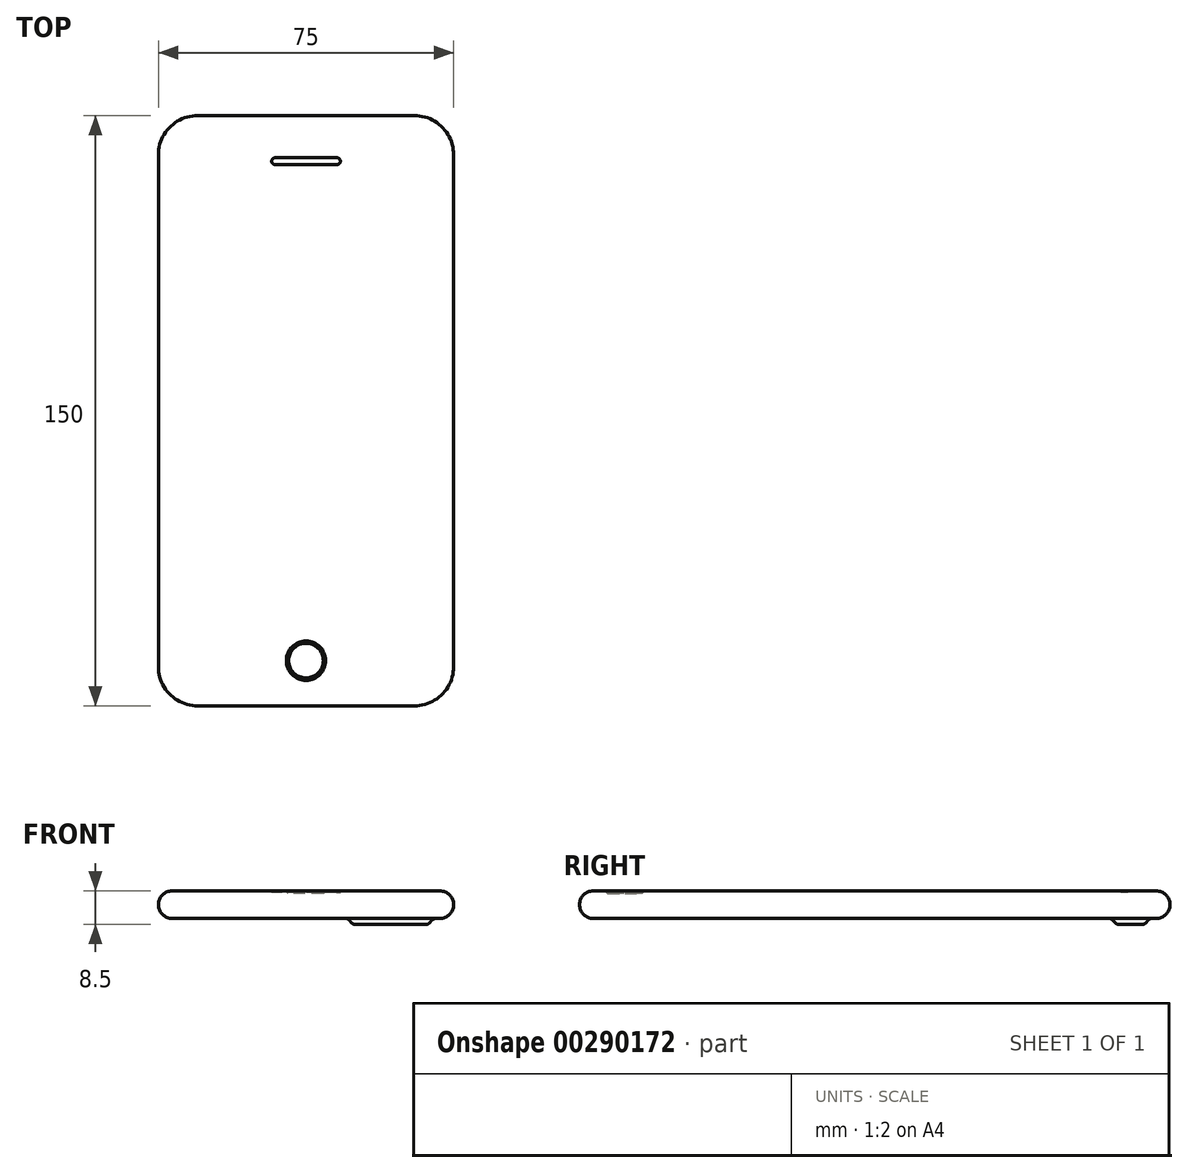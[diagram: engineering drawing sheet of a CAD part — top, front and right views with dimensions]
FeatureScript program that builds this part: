
annotation { "Feature Type Name" : "Feature", "Feature Type Description" : "" }
export const myFeature = defineFeature(function(context is Context, id is Id, definition is map)
    precondition{}
    {
        {
            var Q0;
            Q0=qCreatedBy(makeId("Top.planeOp"),FACE);
            var sketch = newSketch(context, id + "F0", { "sketchPlane" : qUnion([Q0])});
            skLineSegment(sketch, "E0.bottom", {"start": v(37.5, -75) * mm, "end": v(-37.5, -75) * mm});
            skLineSegment(sketch, "E0.top", {"start": v(37.5, 75) * mm, "end": v(-37.5, 75) * mm});
            skLineSegment(sketch, "E0.left", {"start": v(37.5, -75) * mm, "end": v(37.5, 75) * mm});
            skLineSegment(sketch, "E0.right", {"start": v(-37.5, -75) * mm, "end": v(-37.5, 75) * mm});
            skPoint(sketch, "E0.middle", {"position": v(0, 0) * mm});
            skSolve(sketch);
        }
        {
            var Q0;
            Q0 = qSketchRegion(id + "F0", true);
            extrude(context, id + "F1", {"entities" : qUnion([Q0]), "depth" : 7 * mm});
        }
        {
            var Q0;
            Q0=makeQuery(id+"F1.opExtrude","SWEPT_EDGE",EDGE,{"disambiguationData":[OSD([sQuery(id+"F0.wireOp",EDGE,"E0.bottom"),sQuery(id+"F0.wireOp",EDGE,"E0.right")])]});
            var Q1;
            Q1=makeQuery(id+"F1.opExtrude","SWEPT_EDGE",EDGE,{"disambiguationData":[OSD([sQuery(id+"F0.wireOp",EDGE,"E0.bottom"),sQuery(id+"F0.wireOp",EDGE,"E0.left")])]});
            var Q2;
            Q2=makeQuery(id+"F1.opExtrude","SWEPT_EDGE",EDGE,{"disambiguationData":[OSD([sQuery(id+"F0.wireOp",EDGE,"E0.top"),sQuery(id+"F0.wireOp",EDGE,"E0.left")])]});
            var Q3;
            Q3=makeQuery(id+"F1.opExtrude","SWEPT_EDGE",EDGE,{"disambiguationData":[OSD([sQuery(id+"F0.wireOp",EDGE,"E0.top"),sQuery(id+"F0.wireOp",EDGE,"E0.right")])]});
            fillet(context, id + "F2", {"entities" : qUnion([Q0, Q1, Q2, Q3]), "radius" : 10 * mm, "tangentPropagation" : true, "allowEdgeOverflow" : false});
        }
        {
            var Q0;
            Q0=makeQuery(id+"F1.opExtrude","CAP_FACE",FACE,{"disambiguationData":[OSD([sQuery(id+"F0.wireOp",EDGE,"E0.bottom"),sQuery(id+"F0.wireOp",EDGE,"E0.top"),sQuery(id+"F0.wireOp",EDGE,"E0.left"),sQuery(id+"F0.wireOp",EDGE,"E0.right")])],"isStart":true});
            var Q1;
            Q1=makeQuery(id+"F1.opExtrude","CAP_FACE",FACE,{"disambiguationData":[OSD([sQuery(id+"F0.wireOp",EDGE,"E0.bottom"),sQuery(id+"F0.wireOp",EDGE,"E0.top"),sQuery(id+"F0.wireOp",EDGE,"E0.left"),sQuery(id+"F0.wireOp",EDGE,"E0.right")])],"isStart":false});
            fillet(context, id + "F3", {"entities" : qUnion([Q0, Q1]), "radius" : 3.5 * mm, "tangentPropagation" : true, "allowEdgeOverflow" : false});
        }
        {
            var Q0;
            Q0=makeQuery(id+"F1.opExtrude","CAP_FACE",FACE,{"disambiguationData":[OSD([sQuery(id+"F0.wireOp",EDGE,"E0.bottom"),sQuery(id+"F0.wireOp",EDGE,"E0.top"),sQuery(id+"F0.wireOp",EDGE,"E0.left"),sQuery(id+"F0.wireOp",EDGE,"E0.right")])],"isStart":false});
            var sketch = newSketch(context, id + "F4", { "sketchPlane" : qUnion([Q0])});
            skCircle(sketch, "E1", {"center": v(0, -63.5) * mm, "radius": 5 * mm});
            skSolve(sketch);
        }
        {
            var Q0;
            Q0 = qSketchRegion(id + "F4", true);
            extrude(context, id + "F5", {"entities" : qUnion([Q0]), "operationType" : NewBodyOperationType.REMOVE, "oppositeDirection" : true, "depth" : 0.6 * mm});
        }
        {
            var Q0;
            Q0=makeQuery(id+"F5.boolean.opBoolean","COPY",FACE,{"derivedFrom":makeQuery(id+"F5.opExtrude","CAP_FACE",FACE,{"disambiguationData":[OSD([sQuery(id+"F4.wireOp",EDGE,"E1")])],"isStart":false})});
            chamfer(context, id + "F6", {"entities" : qUnion([Q0]), "width" : .6 * mm, "tangentPropagation" : true});
        }
        {
            var Q0;
            Q0=makeQuery(id+"F1.opExtrude","CAP_FACE",FACE,{"disambiguationData":[OSD([sQuery(id+"F0.wireOp",EDGE,"E0.bottom"),sQuery(id+"F0.wireOp",EDGE,"E0.top"),sQuery(id+"F0.wireOp",EDGE,"E0.left"),sQuery(id+"F0.wireOp",EDGE,"E0.right")])],"isStart":false});
            var sketch = newSketch(context, id + "F7", { "sketchPlane" : qUnion([Q0])});
            skLineSegment(sketch, "E2.bottom", {"start": v(8.75, 64.3) * mm, "end": v(-8.75, 64.3) * mm});
            skLineSegment(sketch, "E2.top", {"start": v(8.75, 62.5) * mm, "end": v(-8.75, 62.5) * mm});
            skLineSegment(sketch, "E2.left", {"start": v(8.75, 64.3) * mm, "end": v(8.75, 62.5) * mm});
            skLineSegment(sketch, "E2.right", {"start": v(-8.75, 64.3) * mm, "end": v(-8.75, 62.5) * mm});
            skPoint(sketch, "E2.middle", {"position": v(0, 63.4) * mm});
            skSolve(sketch);
        }
        {
            var Q0;
            Q0 = qSketchRegion(id + "F7", true);
            extrude(context, id + "F8", {"entities" : qUnion([Q0]), "operationType" : NewBodyOperationType.REMOVE, "oppositeDirection" : true, "depth" : .4 * mm});
        }
        {
            var Q0;
            Q0=makeQuery(id+"F8.boolean.opBoolean","COPY",EDGE,{"derivedFrom":makeQuery(id+"F8.opExtrude","SWEPT_EDGE",EDGE,{"disambiguationData":[OSD([sQuery(id+"F7.wireOp",EDGE,"E2.bottom"),sQuery(id+"F7.wireOp",EDGE,"E2.left")])]})});
            var Q1;
            Q1=makeQuery(id+"F8.boolean.opBoolean","COPY",EDGE,{"derivedFrom":makeQuery(id+"F8.opExtrude","SWEPT_EDGE",EDGE,{"disambiguationData":[OSD([sQuery(id+"F7.wireOp",EDGE,"E2.top"),sQuery(id+"F7.wireOp",EDGE,"E2.left")])]})});
            var Q2;
            Q2=makeQuery(id+"F8.boolean.opBoolean","COPY",EDGE,{"derivedFrom":makeQuery(id+"F8.opExtrude","SWEPT_EDGE",EDGE,{"disambiguationData":[OSD([sQuery(id+"F7.wireOp",EDGE,"E2.bottom"),sQuery(id+"F7.wireOp",EDGE,"E2.right")])]})});
            var Q3;
            Q3=makeQuery(id+"F8.boolean.opBoolean","COPY",EDGE,{"derivedFrom":makeQuery(id+"F8.opExtrude","SWEPT_EDGE",EDGE,{"disambiguationData":[OSD([sQuery(id+"F7.wireOp",EDGE,"E2.top"),sQuery(id+"F7.wireOp",EDGE,"E2.right")])]})});
            fillet(context, id + "F9", {"entities" : qUnion([Q0, Q1, Q2, Q3]), "radius" : 1 * mm, "tangentPropagation" : true, "allowEdgeOverflow" : false});
        }
        {
            var Q0;
            Q0=makeQuery(id+"F1.opExtrude","CAP_FACE",FACE,{"disambiguationData":[OSD([sQuery(id+"F0.wireOp",EDGE,"E0.bottom"),sQuery(id+"F0.wireOp",EDGE,"E0.top"),sQuery(id+"F0.wireOp",EDGE,"E0.left"),sQuery(id+"F0.wireOp",EDGE,"E0.right")])],"isStart":true});
            var sketch = newSketch(context, id + "F10", { "sketchPlane" : qUnion([Q0])});
            skLineSegment(sketch, "E3.bottom", {"start": v(15.5, -70) * mm, "end": v(27.5, -70) * mm});
            skLineSegment(sketch, "E3.top", {"start": v(15.5, -60) * mm, "end": v(27.5, -60) * mm});
            skLineSegment(sketch, "E3.left", {"start": v(10.5, -65) * mm, "end": v(10.5, -65) * mm});
            skLineSegment(sketch, "E3.right", {"start": v(32.5, -65) * mm, "end": v(32.5, -65) * mm});
            skPoint(sketch, "E3.middle", {"position": v(21.5, -65) * mm});
            skPoint(sketch, "E4.visualSharp", {"position": v(32.5, -70) * mm});
            skArc(sketch, "E4.filletArc", {"start": v(27.5, -70) * mm, "mid": v(31.04, -68.54) * mm, "end": v(32.5, -65) * mm});
            skPoint(sketch, "E5.visualSharp", {"position": v(32.5, -60) * mm});
            skArc(sketch, "E5.filletArc", {"start": v(32.5, -65) * mm, "mid": v(31.04, -61.46) * mm, "end": v(27.5, -60) * mm});
            skPoint(sketch, "E6.visualSharp", {"position": v(10.5, -70) * mm});
            skArc(sketch, "E6.filletArc", {"start": v(10.5, -65) * mm, "mid": v(11.96, -68.54) * mm, "end": v(15.5, -70) * mm});
            skPoint(sketch, "E7.visualSharp", {"position": v(10.5, -60) * mm});
            skArc(sketch, "E7.filletArc", {"start": v(15.5, -60) * mm, "mid": v(11.96, -61.46) * mm, "end": v(10.5, -65) * mm});
            skSolve(sketch);
        }
        {
            var Q0;
            Q0 = qSketchRegion(id + "F10", true);
            extrude(context, id + "F11", {"entities" : qUnion([Q0]), "operationType" : NewBodyOperationType.ADD, "depth" : 1.5 * mm});
        }
        {
            var Q0;
            Q0=makeQuery(id+"F11.opExtrude","CAP_EDGE",EDGE,{"disambiguationData":[OSD([sQuery(id+"F10.wireOp",EDGE,"E3.bottom")])],"isStart":false});
            chamfer(context, id + "F12", {"entities" : qUnion([Q0]), "width" : 1.5 * mm, "tangentPropagation" : true});
        }
        {
            var Q0;
            Q0=makeQuery(id+"F12.opChamfer","BLEND_EDGE",EDGE,{"blendedFrom":[makeQuery(id+"F11.opExtrude","CAP_EDGE",EDGE,{"disambiguationData":[OSD([sQuery(id+"F10.wireOp",EDGE,"E3.bottom")])],"isStart":false}),makeQuery(id+"F1.opExtrude","CAP_FACE",FACE,{"disambiguationData":[OSD([sQuery(id+"F0.wireOp",EDGE,"E0.bottom"),sQuery(id+"F0.wireOp",EDGE,"E0.top"),sQuery(id+"F0.wireOp",EDGE,"E0.left"),sQuery(id+"F0.wireOp",EDGE,"E0.right")])],"isStart":true})],"blendedInto":[makeQuery(id+"F1.opExtrude","CAP_FACE",FACE,{"disambiguationData":[OSD([sQuery(id+"F0.wireOp",EDGE,"E0.bottom"),sQuery(id+"F0.wireOp",EDGE,"E0.top"),sQuery(id+"F0.wireOp",EDGE,"E0.left"),sQuery(id+"F0.wireOp",EDGE,"E0.right")])],"isStart":true})]});
            var Q1;
            {var subQ0=sQuery(id+"F10.wireOp",EDGE,"E3.bottom");Q1=makeQuery(id+"F12.opChamfer","BLEND_EDGE",EDGE,{"blendedFrom":[makeQuery(id+"F11.opExtrude","CAP_EDGE",EDGE,{"disambiguationData":[OSD([subQ0])],"isStart":false}),makeQuery(id+"F11.opExtrude","CAP_FACE",FACE,{"disambiguationData":[OSD([subQ0,sQuery(id+"F10.wireOp",EDGE,"E3.top"),sQuery(id+"F10.wireOp",EDGE,"E4.filletArc"),sQuery(id+"F10.wireOp",EDGE,"E5.filletArc"),sQuery(id+"F10.wireOp",EDGE,"E6.filletArc"),sQuery(id+"F10.wireOp",EDGE,"E7.filletArc")])],"isStart":false})],"blendedInto":[makeQuery(id+"F11.opExtrude","CAP_FACE",FACE,{"disambiguationData":[OSD([subQ0,sQuery(id+"F10.wireOp",EDGE,"E3.top"),sQuery(id+"F10.wireOp",EDGE,"E4.filletArc"),sQuery(id+"F10.wireOp",EDGE,"E5.filletArc"),sQuery(id+"F10.wireOp",EDGE,"E6.filletArc"),sQuery(id+"F10.wireOp",EDGE,"E7.filletArc")])],"isStart":false})]});}
            fillet(context, id + "F13", {"entities" : qUnion([Q0, Q1]), "radius" : 1 * mm, "tangentPropagation" : true, "allowEdgeOverflow" : false});
        }
    });
